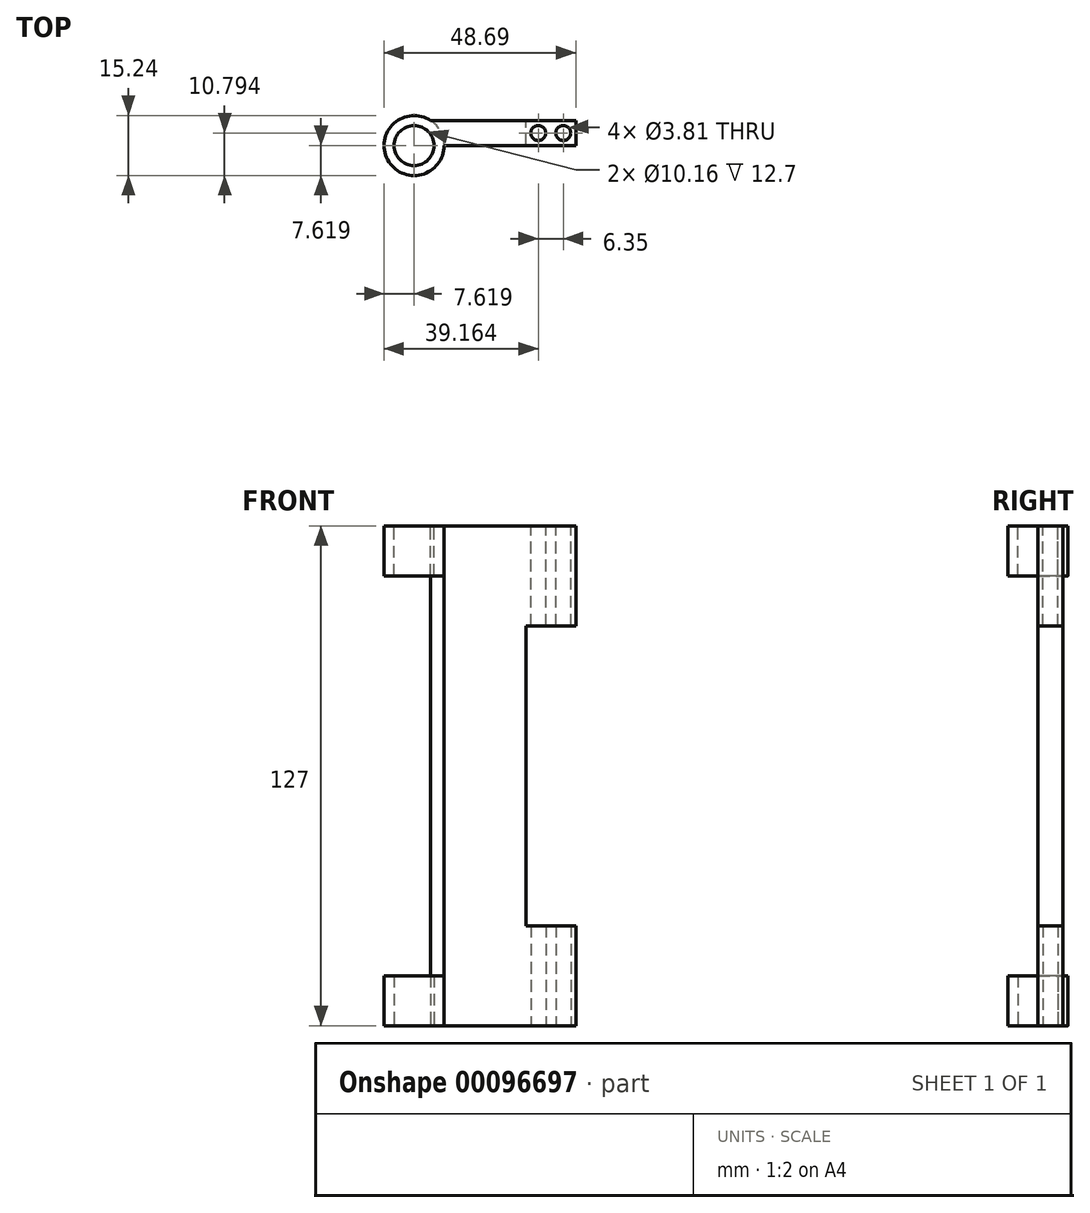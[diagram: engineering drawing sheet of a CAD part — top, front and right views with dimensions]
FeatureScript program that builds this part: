
annotation { "Feature Type Name" : "Feature", "Feature Type Description" : "" }
export const myFeature = defineFeature(function(context is Context, id is Id, definition is map)
    precondition{}
    {
        {
            var Q0;
            Q0=qCreatedBy(makeId("Top.planeOp"),FACE);
            var sketch = newSketch(context, id + "F0", { "sketchPlane" : qUnion([Q0])});
            skLineSegment(sketch, "E0", {"start": v(-20.3, -33.32) * mm, "end": v(-33, -33.32) * mm});
            skLineSegment(sketch, "E1", {"start": v(-20.3, -26.97) * mm, "end": v(-61.36, -26.97) * mm});
            skLineSegment(sketch, "E2.MirrorCS", {"start": v(-20.3, -20.62) * mm, "end": v(-33, -20.62) * mm});
            skCircle(sketch, "E3", {"center": v(-61.36, -26.97) * mm, "radius": 7.62 * mm});
            skLineSegment(sketch, "E4", {"start": v(-20.3, -20.62) * mm, "end": v(-20.3, -26.97) * mm});
            skLineSegment(sketch, "E5", {"start": v(-20.3, -26.97) * mm, "end": v(-20.3, -33.32) * mm});
            skCircle(sketch, "E6", {"center": v(-61.36, -26.97) * mm, "radius": 5.08 * mm});
            skLineSegment(sketch, "E7", {"start": v(-33, -20.62) * mm, "end": v(-57.15, -20.62) * mm});
            skLineSegment(sketch, "E8", {"start": v(-33, -33.32) * mm, "end": v(-57.15, -33.32) * mm});
            skLineSegment(sketch, "E9", {"start": v(-33, -20.62) * mm, "end": v(-33, -26.97) * mm});
            skLineSegment(sketch, "E10", {"start": v(-33, -26.97) * mm, "end": v(-33, -33.32) * mm});
            skCircle(sketch, "E11", {"center": v(-29.82, -23.8) * mm, "radius": 1.9 * mm});
            skCircle(sketch, "E12.MirrorC", {"center": v(-23.47, -23.8) * mm, "radius": 1.9 * mm});
            skCircle(sketch, "E13.MirrorC", {"center": v(-29.82, -30.15) * mm, "radius": 1.9 * mm});
            skCircle(sketch, "E14.MirrorC", {"center": v(-23.47, -30.15) * mm, "radius": 1.9 * mm});
            skLineSegment(sketch, "E15", {"start": v(-26.64, -20.62) * mm, "end": v(-26.64, -26.97) * mm});
            skLineSegment(sketch, "E16", {"start": v(-26.64, -26.97) * mm, "end": v(-26.64, -33.32) * mm});
            skSolve(sketch);
        }
        {
            var Q0;
            Q0=makeQuery(id+"F0.imprint","IMPRINT",FACE,{"disambiguationData":[TD([[makeQuery(id+"F0.imprint","IMPRINT",EDGE,{"derivedFrom":sQuery(id+"F0.wireOp",EDGE,"E6")}),-1.0]])]});
            extrude(context, id + "F1", {"entities" : qUnion([Q0]), "depth" : 12.7 * mm});
        }
        {
            var Q0;
            {var subQ4=sQuery(id+"F0.wireOp",EDGE,"E7");Q0=makeQuery(id+"F0.imprint","IMPRINT",FACE,{"disambiguationData":[TD([[makeQuery(id+"F0.imprint","IMPRINT",EDGE,{"derivedFrom":subQ4}),1.0]])]});}
            var Q1;
            Q1=makeQuery(id+"F0.imprint","IMPRINT",FACE,{"disambiguationData":[TD([[makeQuery(id+"F0.imprint","IMPRINT",EDGE,{"derivedFrom":sQuery(id+"F0.wireOp",EDGE,"E2.MirrorCS")}),1.0]])]});
            extrude(context, id + "F2", {"entities" : qUnion([Q0, Q1]), "operationType" : NewBodyOperationType.ADD, "depth" : 25.4 * mm});
        }
        {
            var Q0;
            {var subQ4=sQuery(id+"F0.wireOp",EDGE,"E7");Q0=makeQuery(id+"F0.imprint","IMPRINT",FACE,{"disambiguationData":[TD([[makeQuery(id+"F0.imprint","IMPRINT",EDGE,{"derivedFrom":subQ4}),1.0]])]});}
            extrude(context, id + "F3", {"entities" : qUnion([Q0]), "operationType" : NewBodyOperationType.ADD, "depth" : 63.5 * mm});
        }
        {
            var Q0;
            Q0=makeQuery(id+"F1.opExtrude","SWEPT_BODY",BODY,{"disambiguationData":[OSD([sQuery(id+"F0.wireOp",EDGE,"E3"),sQuery(id+"F0.wireOp",EDGE,"E6")])]});
            var Q1;
            Q1=makeQuery(id+"F3.opExtrude","CAP_FACE",FACE,{"disambiguationData":[OSD([sQuery(id+"F0.wireOp",EDGE,"E1"),sQuery(id+"F0.wireOp",EDGE,"E3"),sQuery(id+"F0.wireOp",EDGE,"E7"),sQuery(id+"F0.wireOp",EDGE,"E9")])],"isStart":false});
            mirror(context, id + "F4", {"operationType" : NewBodyOperationType.ADD, "entities" : qUnion([Q0]), "mirrorPlane" : qUnion([Q1])});
        }
    });
